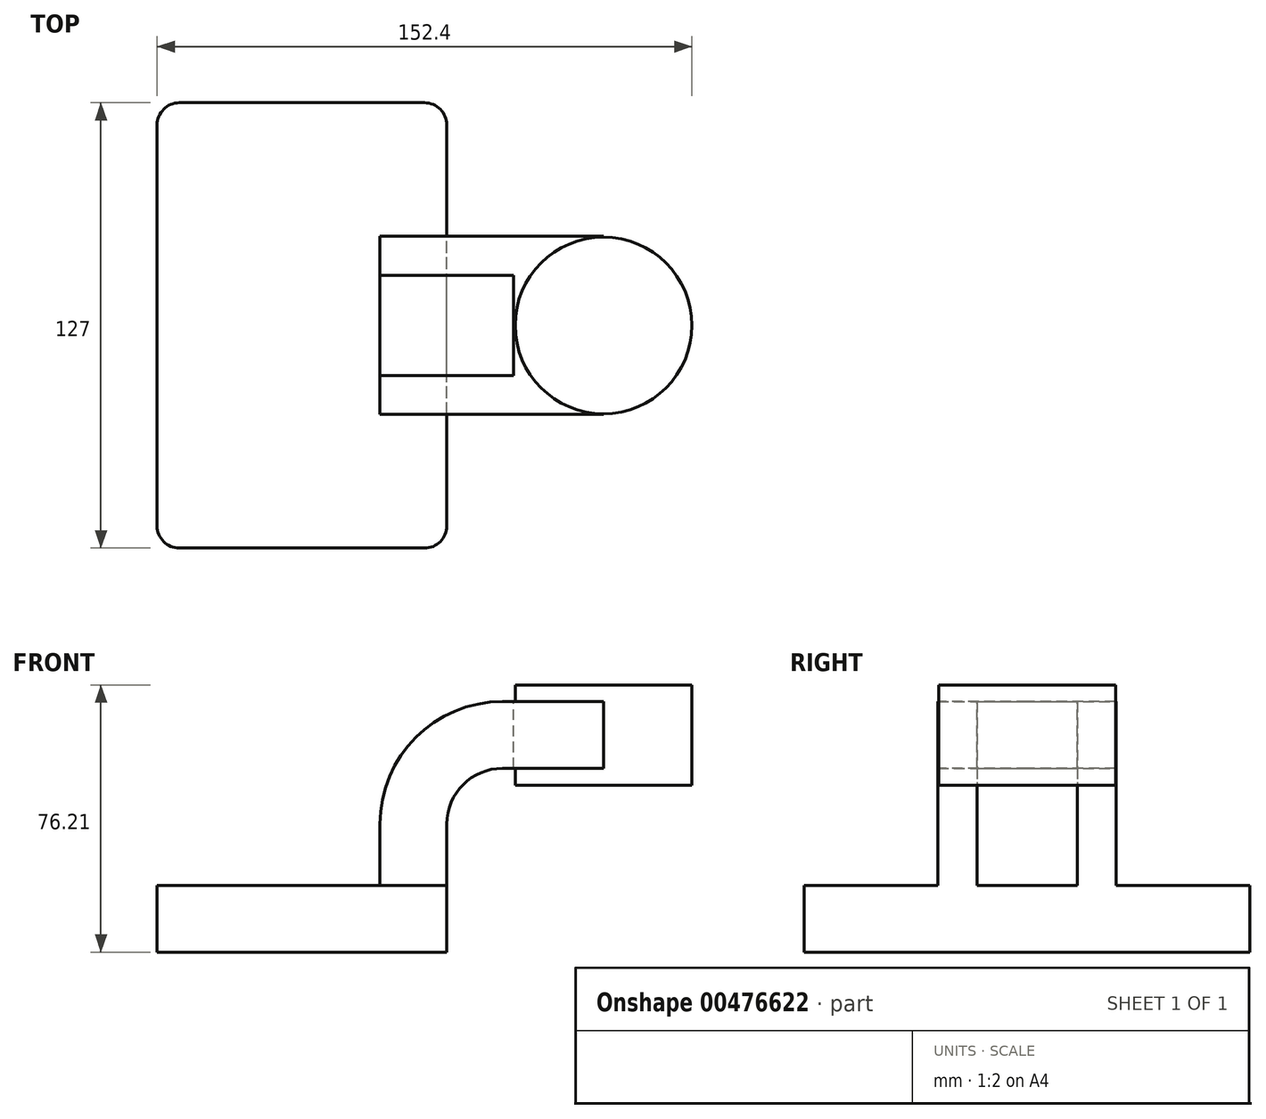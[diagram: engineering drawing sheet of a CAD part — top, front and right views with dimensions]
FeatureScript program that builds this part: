
annotation { "Feature Type Name" : "Feature", "Feature Type Description" : "" }
export const myFeature = defineFeature(function(context is Context, id is Id, definition is map)
    precondition{}
    {
        {
            var Q0;
            Q0=qCreatedBy(makeId("Front.planeOp"),FACE);
            var sketch = newSketch(context, id + "F0", { "sketchPlane" : qUnion([Q0])});
            skLineSegment(sketch, "E0.bottom", {"start": v(-41.28, -9.53) * mm, "end": v(41.28, -9.53) * mm});
            skLineSegment(sketch, "E0.top", {"start": v(-41.28, 9.53) * mm, "end": v(41.27, 9.53) * mm});
            skLineSegment(sketch, "E0.left", {"start": v(-41.27, -9.53) * mm, "end": v(-41.28, 9.53) * mm});
            skLineSegment(sketch, "E0.right", {"start": v(41.28, -9.53) * mm, "end": v(41.27, 9.53) * mm});
            skPoint(sketch, "E0.middle", {"position": v(0, 0) * mm});
            skLineSegment(sketch, "E1.bottom", {"start": v(111.12, 38.1) * mm, "end": v(60.33, 38.1) * mm});
            skLineSegment(sketch, "E1.top", {"start": v(111.13, 66.67) * mm, "end": v(60.33, 66.67) * mm});
            skLineSegment(sketch, "E1.left", {"start": v(111.13, 38.1) * mm, "end": v(111.13, 66.67) * mm});
            skLineSegment(sketch, "E1.right", {"start": v(60.33, 38.1) * mm, "end": v(60.33, 66.67) * mm});
            skPoint(sketch, "E1.middle", {"position": v(85.73, 52.39) * mm});
            skLineSegment(sketch, "E2", {"start": v(41.27, 9.52) * mm, "end": v(41.27, 27) * mm});
            skArc(sketch, "E3", {"start": v(41.27, 27) * mm, "mid": v(45.92, 38.23) * mm, "end": v(57.15, 42.88) * mm});
            skLineSegment(sketch, "E4", {"start": v(57.15, 42.88) * mm, "end": v(85.94, 42.88) * mm});
            skLineSegment(sketch, "E5.0", {"start": v(57.15, 61.93) * mm, "end": v(85.94, 61.93) * mm});
            skArc(sketch, "E5.1", {"start": v(22.22, 27) * mm, "mid": v(32.45, 51.7) * mm, "end": v(57.15, 61.93) * mm});
            skLineSegment(sketch, "E5.2", {"start": v(22.22, 9.52) * mm, "end": v(22.22, 27) * mm});
            skLineSegment(sketch, "E6", {"start": v(85.94, 42.88) * mm, "end": v(85.94, 61.93) * mm});
            skLineSegment(sketch, "E7", {"start": v(85.94, 61.93) * mm, "end": v(85.94, 38.1) * mm});
            skLineSegment(sketch, "E8", {"start": v(85.94, 38.1) * mm, "end": v(85.94, 66.67) * mm});
            skFitSpline(sketch, "E9", {"points": [v(-41.28, 9.53) * mm, v(57.15, 61.93) * mm], "startDerivative": vector(166.22, 54.5) * mm, "endDerivative": vector(105, -17.6) * mm});
            skSolve(sketch);
        }
        {
            var Q0;
            Q0=makeQuery(id+"F0.imprint","IMPRINT",FACE,{"disambiguationData":[TD([[makeQuery(id+"F0.imprint","IMPRINT",EDGE,{"derivedFrom":sQuery(id+"F0.wireOp",EDGE,"E0.bottom")}),1.0]])]});
            extrude(context, id + "F1", {"entities" : qUnion([Q0]), "endBound" : BoundingType.SYMMETRIC, "depth" : 127 * mm});
        }
        {
            var Q0;
            {var subQ0=sQuery(id+"F0.wireOp",EDGE,"E4");var subQ1=sQuery(id+"F0.wireOp",EDGE,"E1.right");var subQ2=makeQuery(id+"F0.imprint","INTERSECT",VERTEX,{"derivedFrom":[subQ1,subQ0]});Q0=makeQuery(id+"F0.imprint","IMPRINT",FACE,{"disambiguationData":[TD([[makeQuery(id+"F0.imprint","IMPRINT",EDGE,{"disambiguationData":[TD([[subQ2,-1.0]])],"derivedFrom":subQ1}),-1.0]])]});}
            var Q1;
            {var subQ1=sQuery(id+"F0.wireOp",EDGE,"E2");Q1=makeQuery(id+"F0.imprint","IMPRINT",FACE,{"disambiguationData":[TD([[makeQuery(id+"F0.imprint","IMPRINT",EDGE,{"derivedFrom":subQ1}),1.0]])]});}
            extrude(context, id + "F2", {"entities" : qUnion([Q0, Q1]), "endBound" : BoundingType.SYMMETRIC, "depth" : 50.8 * mm});
        }
        {
            var Q0;
            Q0=makeQuery(id+"F0.imprint","IMPRINT",FACE,{"disambiguationData":[TD([[makeQuery(id+"F0.imprint","IMPRINT",EDGE,{"derivedFrom":sQuery(id+"F0.wireOp",EDGE,"E5.1")}),1.0]])]});
            extrude(context, id + "F3", {"entities" : qUnion([Q0]), "operationType" : NewBodyOperationType.ADD, "endBound" : BoundingType.SYMMETRIC, "depth" : 15.88 * mm});
        }
        {
            var Q0;
            {var subQ1=sQuery(id+"F0.wireOp",EDGE,"E2");Q0=makeQuery(id+"F0.imprint","IMPRINT",FACE,{"disambiguationData":[TD([[makeQuery(id+"F0.imprint","IMPRINT",EDGE,{"derivedFrom":subQ1}),1.0]])]});}
            extrude(context, id + "F4", {"entities" : qUnion([Q0]), "endBound" : BoundingType.SYMMETRIC, "depth" : 28.57 * mm});
        }
        {
            var Q0;
            {var subQ4=sQuery(id+"F0.wireOp",EDGE,"E1.left");Q0=makeQuery(id+"F0.imprint","IMPRINT",FACE,{"disambiguationData":[TD([[makeQuery(id+"F0.imprint","IMPRINT",EDGE,{"derivedFrom":subQ4}),1.0]])]});}
            var Q1;
            Q1=sQuery(id+"F0.wireOp",EDGE,"E8");
            revolve(context, id + "F5", {"operationType" : NewBodyOperationType.ADD, "entities" : qUnion([Q0]), "axis" : qUnion([Q1]), "revolveType" : RevolveType.FULL});
        }
        {
            var Q0;
            Q0=makeQuery(id+"F1.opExtrude","CAP_EDGE",EDGE,{"disambiguationData":[OSD([sQuery(id+"F0.wireOp",EDGE,"E0.right")])],"isStart":false});
            var Q1;
            Q1=makeQuery(id+"F1.opExtrude","CAP_EDGE",EDGE,{"disambiguationData":[OSD([sQuery(id+"F0.wireOp",EDGE,"E0.left")])],"isStart":false});
            var Q2;
            Q2=makeQuery(id+"F1.opExtrude","CAP_EDGE",EDGE,{"disambiguationData":[OSD([sQuery(id+"F0.wireOp",EDGE,"E0.right")])],"isStart":true});
            var Q3;
            Q3=makeQuery(id+"F1.opExtrude","CAP_EDGE",EDGE,{"disambiguationData":[OSD([sQuery(id+"F0.wireOp",EDGE,"E0.left")])],"isStart":true});
            fillet(context, id + "F6", {"entities" : qUnion([Q0, Q1, Q2, Q3]), "radius" : 6.35 * mm, "tangentPropagation" : true, "allowEdgeOverflow" : false});
        }
    });
